# Revit family: Urinal-Hybrid-Sloan-HYB-1000_Series
name_source: partatom
category: Plumbing Fixtures
revit_build: Autodesk Revit 2014 (Build: 20130308_1515(x64)
units: mm (PartAtom-declared; Revit-internal decimal feet)

## types (1)
- HYB-1000
    ADA Compliant = Yes
    Assembly Code = D2010210
    CW Connection = Yes
    CWFU = 0
    Default Elevation = 24"
    Description = Complete Vitreous China Hybrid Urinal
    Fixture Color = White
    Flush Choice = Hybrid
    Flush Volumes and Flow Rates = Waterfree
    HW Connection = No
    HWFU = 0
    Height = 38 1/4"
    Length = 14 3/8"
    Manufacturer = SLOAN
    Material = Vitreous China-Sloan-White
    Model = HYB-1000
    Mounting = Wall Hung
    Order Code = 1001020
    Price = Prices may vary. Please consult Sloan Rep for most up-to-date price list.
    Product Documentation Link = https://specifications.sloan.com
    Product Page URL = https://www.sloan.com
    URL = www.sloan.com
    Vent Connection = No
    WFU = 5
    Warranty Information = 3 Year (Limited)
    Waste Connection = Yes
    Waste Connection Diameter = 2"
    Waste Connection Height = 16 3/4"
    Waste Connection Radius = 1"
    Width = 16 5/8"

## geometry (parser evidence)
native form markers: Sweep x1
no freeform markers — native parametric forms only
